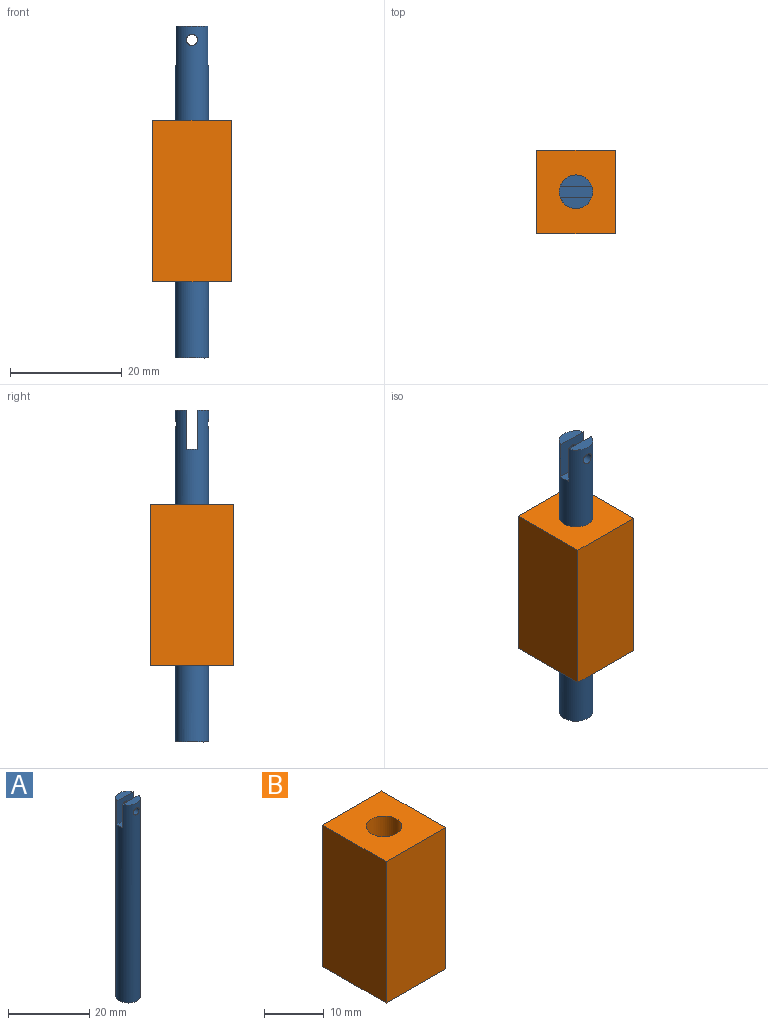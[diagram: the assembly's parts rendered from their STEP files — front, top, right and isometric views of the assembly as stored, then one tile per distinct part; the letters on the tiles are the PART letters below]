
ASSEMBLY  parts=2 mates=1
PART A: 9 faces, bbox 6x6x59.5 mm
  f0: cylinder r=3mm len=59.5mm, axis (0,0,-1), area 1086.6mm2, adj f1,f2,f3,f4,f5,f6,f7,f8
  f1: plane 6x2mm, normal (0,0,1), area 11.8mm2, adj f0,f3,f5
  f2: plane 6x6mm, normal (0,0,-1), area 28.3mm2, adj f0
  f3: plane 7x5.66mm, normal (0,-1,0), area 36.5mm2, adj f0,f1,f4,f8
  f4: plane 5.66x2mm, normal (0,0,1), area 8.3mm2, adj f0,f3
  f5: plane 7x5.66mm, normal (0,1,0), area 36.5mm2, adj f0,f1,f6,f7
  f6: plane 5.66x2mm, normal (0,0,1), area 8.3mm2, adj f0,f5
  f7: cylinder r=1mm len=2mm, axis (0,-1,0), area 12mm2, adj f0,f5
  f8: cylinder r=1mm len=2mm, axis (0,-1,0), area 12mm2, adj f0,f3
PART B: 11 faces, bbox 14x15x29 mm
  f0: plane 29x14mm, normal (0,1,0), area 388.9mm2, adj f1,f2,f3,f4,f6,f9
  f1: plane 15x14mm, normal (0,0,1), area 181.7mm2, adj f0,f2,f4,f5,f10
  f2: plane 29x15mm, normal (-1,0,0), area 435mm2, adj f0,f1,f3,f5
  f3: plane 15x14mm, normal (0,0,-1), area 181.7mm2, adj f0,f2,f4,f5,f10
  f4: plane 29x15mm, normal (1,0,0), area 435mm2, adj f0,f1,f3,f5
  f5: plane 29x14mm, normal (0,-1,0), area 406mm2, adj f1,f2,f3,f4
  f6: cylinder r=1.65mm len=3.3mm, axis (0,-1,0), area 10.4mm2, adj f0,f7
  f7: plane 3.3x3.3mm, normal (0,1,0), area 8.6mm2, adj f6
  f8: plane 3.3x3.3mm, normal (0,1,0), area 8.6mm2, adj f9
  f9: cylinder r=1.65mm len=3.3mm, axis (0,-1,0), area 10.4mm2, adj f0,f8
  f10: cylinder r=3mm len=29mm, axis (0,0,1), area 546.6mm2, adj f1,f3
PLACE A t=(5.08,-3.77,-0.82)mm
PLACE B t=(5.08,-3.77,-1.17)mm
MATE slider A.f0 <-> B.f10  axis (0,0,-1) through (5.08,-3.77,0.43)mm
